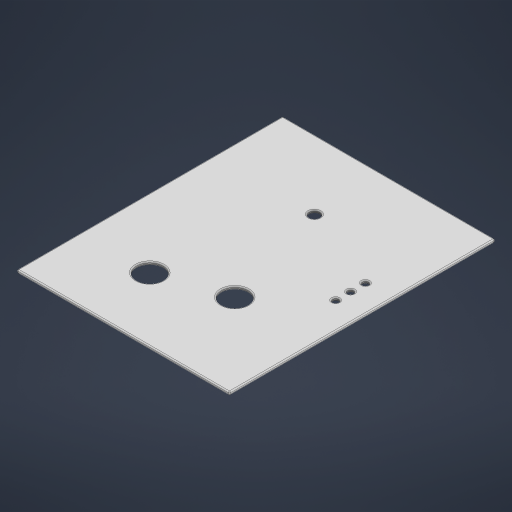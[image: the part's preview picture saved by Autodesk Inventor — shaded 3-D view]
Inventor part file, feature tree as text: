
AUTODESK INVENTOR PART (.ipt)
format: ipt  version: 2023 (Build 270158000, 158)  size: 256,000 bytes
history: native  units: mm
features: fillet x1, other x1
ambient origin geometry x8: Origin, YZ Plane, XZ Plane, XY Plane, X Axis, Y Axis, Z Axis, Center Point
bodies: Solid1 (feature_tree)
feature tree (2):
  fillet  "Fillet1"  Radius=200.0mm
  other  "page_lines"
